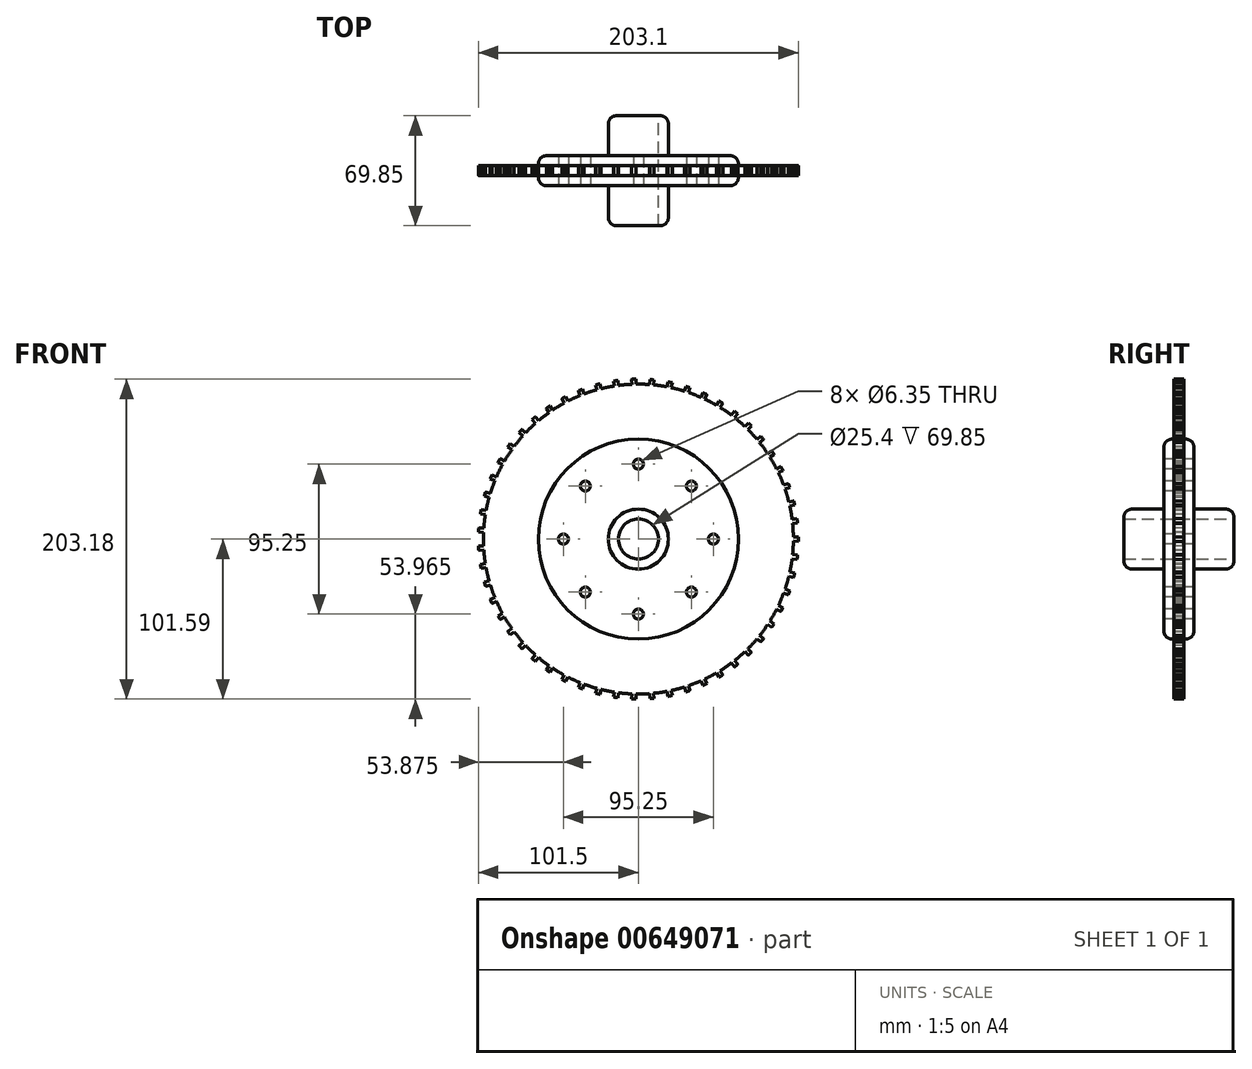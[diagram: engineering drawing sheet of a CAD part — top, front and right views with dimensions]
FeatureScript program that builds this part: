
annotation { "Feature Type Name" : "Feature", "Feature Type Description" : "" }
export const myFeature = defineFeature(function(context is Context, id is Id, definition is map)
    precondition{}
    {
        {
            var Q0;
            Q0=qCreatedBy(makeId("Front.planeOp"),FACE);
            var sketch = newSketch(context, id + "F0", { "sketchPlane" : qUnion([Q0])});
            skCircle(sketch, "E0", {"center": v(0, 0) * mm, "radius": 101.6 * mm});
            skCircle(sketch, "E1", {"center": v(0, 0) * mm, "radius": 12.7 * mm});
            skSolve(sketch);
        }
        {
            var Q0;
            Q0 = qSketchRegion(id + "F0", true);
            extrude(context, id + "F1", {"entities" : qUnion([Q0]), "depth" : 6.35 * mm, "offsetDistance" : 25.4 * mm});
        }
        {
            var Q0;
            Q0=makeQuery(id+"F1.opExtrude","CAP_FACE",FACE,{"disambiguationData":[OSD([sQuery(id+"F0.wireOp",EDGE,"E0"),sQuery(id+"F0.wireOp",EDGE,"E1")])],"isStart":false});
            var sketch = newSketch(context, id + "F2", { "sketchPlane" : qUnion([Q0])});
            skArc(sketch, "E2", {"start": v(-101.5, 4.43) * mm, "mid": v(-101.6, 0) * mm, "end": v(-101.5, -4.43) * mm});
            skArc(sketch, "E3", {"start": v(-98.33, 4.3) * mm, "mid": v(-98.43, 0) * mm, "end": v(-98.33, -4.3) * mm});
            skLineSegment(sketch, "E4", {"start": v(-98.33, -4.3) * mm, "end": v(-101.5, -4.43) * mm});
            skLineSegment(sketch, "E5", {"start": v(-101.5, -4.43) * mm, "end": v(-98.33, -4.3) * mm});
            skLineSegment(sketch, "E6", {"start": v(-101.5, 4.43) * mm, "end": v(-98.33, 4.3) * mm});
            skArc(sketch, "E7.1.0", {"start": v(-98.18, -6.94) * mm, "mid": v(-97.78, -11.22) * mm, "end": v(-97.2, -15.47) * mm});
            skLineSegment(sketch, "E7.1.1", {"start": v(-100.34, -15.97) * mm, "end": v(-97.2, -15.47) * mm});
            skLineSegment(sketch, "E7.1.2", {"start": v(-101.35, -7.17) * mm, "end": v(-98.18, -6.94) * mm});
            skArc(sketch, "E7.1.3", {"start": v(-101.35, -7.17) * mm, "mid": v(-100.94, -11.58) * mm, "end": v(-100.34, -15.97) * mm});
            skArc(sketch, "E7.2.0", {"start": v(-96.75, -18.1) * mm, "mid": v(-95.87, -22.3) * mm, "end": v(-94.8, -26.45) * mm});
            skLineSegment(sketch, "E7.2.1", {"start": v(-97.86, -27.3) * mm, "end": v(-94.8, -26.45) * mm});
            skLineSegment(sketch, "E7.2.2", {"start": v(-99.87, -18.67) * mm, "end": v(-96.75, -18.1) * mm});
            skArc(sketch, "E7.2.3", {"start": v(-99.87, -18.67) * mm, "mid": v(-98.96, -23.01) * mm, "end": v(-97.86, -27.3) * mm});
            skArc(sketch, "E7.3.0", {"start": v(-94.06, -29) * mm, "mid": v(-92.7, -33.08) * mm, "end": v(-91.17, -37.09) * mm});
            skLineSegment(sketch, "E7.3.1", {"start": v(-94.11, -38.28) * mm, "end": v(-91.17, -37.09) * mm});
            skLineSegment(sketch, "E7.3.2", {"start": v(-97.09, -29.94) * mm, "end": v(-94.06, -29) * mm});
            skArc(sketch, "E7.3.3", {"start": v(-97.09, -29.94) * mm, "mid": v(-95.7, -34.14) * mm, "end": v(-94.11, -38.28) * mm});
            skArc(sketch, "E7.4.0", {"start": v(-90.14, -39.53) * mm, "mid": v(-88.33, -43.43) * mm, "end": v(-86.35, -47.24) * mm});
            skLineSegment(sketch, "E7.4.1", {"start": v(-89.13, -48.76) * mm, "end": v(-86.35, -47.24) * mm});
            skLineSegment(sketch, "E7.4.2", {"start": v(-93.04, -40.8) * mm, "end": v(-90.14, -39.53) * mm});
            skArc(sketch, "E7.4.3", {"start": v(-93.04, -40.8) * mm, "mid": v(-91.18, -44.83) * mm, "end": v(-89.13, -48.76) * mm});
            skArc(sketch, "E7.5.0", {"start": v(-85.04, -49.55) * mm, "mid": v(-82.8, -53.21) * mm, "end": v(-80.4, -56.77) * mm});
            skLineSegment(sketch, "E7.5.1", {"start": v(-83, -58.6) * mm, "end": v(-80.4, -56.77) * mm});
            skLineSegment(sketch, "E7.5.2", {"start": v(-87.79, -51.15) * mm, "end": v(-85.04, -49.55) * mm});
            skArc(sketch, "E7.5.3", {"start": v(-87.79, -51.15) * mm, "mid": v(-85.47, -54.93) * mm, "end": v(-83, -58.6) * mm});
            skArc(sketch, "E7.6.0", {"start": v(-78.84, -58.92) * mm, "mid": v(-76.2, -62.3) * mm, "end": v(-73.4, -65.57) * mm});
            skLineSegment(sketch, "E7.6.1", {"start": v(-75.77, -67.68) * mm, "end": v(-73.4, -65.57) * mm});
            skLineSegment(sketch, "E7.6.2", {"start": v(-81.38, -60.82) * mm, "end": v(-78.84, -58.92) * mm});
            skArc(sketch, "E7.6.3", {"start": v(-81.38, -60.82) * mm, "mid": v(-78.65, -64.31) * mm, "end": v(-75.77, -67.68) * mm});
            skArc(sketch, "E7.7.0", {"start": v(-71.6, -67.52) * mm, "mid": v(-68.6, -70.58) * mm, "end": v(-65.45, -73.5) * mm});
            skLineSegment(sketch, "E7.7.1", {"start": v(-67.56, -75.88) * mm, "end": v(-65.45, -73.5) * mm});
            skLineSegment(sketch, "E7.7.2", {"start": v(-73.92, -69.7) * mm, "end": v(-71.6, -67.52) * mm});
            skArc(sketch, "E7.7.3", {"start": v(-73.92, -69.7) * mm, "mid": v(-70.8, -72.86) * mm, "end": v(-67.56, -75.88) * mm});
            skArc(sketch, "E7.8.0", {"start": v(-63.45, -75.25) * mm, "mid": v(-60.1, -77.94) * mm, "end": v(-56.65, -80.5) * mm});
            skLineSegment(sketch, "E7.8.1", {"start": v(-58.47, -83.09) * mm, "end": v(-56.65, -80.5) * mm});
            skLineSegment(sketch, "E7.8.2", {"start": v(-65.5, -77.67) * mm, "end": v(-63.45, -75.25) * mm});
            skArc(sketch, "E7.8.3", {"start": v(-65.5, -77.67) * mm, "mid": v(-62.04, -80.46) * mm, "end": v(-58.47, -83.09) * mm});
            skArc(sketch, "E7.9.0", {"start": v(-54.45, -81.99) * mm, "mid": v(-50.83, -84.29) * mm, "end": v(-47.1, -86.42) * mm});
            skLineSegment(sketch, "E7.9.1", {"start": v(-48.62, -89.21) * mm, "end": v(-47.1, -86.42) * mm});
            skLineSegment(sketch, "E7.9.2", {"start": v(-56.21, -84.63) * mm, "end": v(-54.45, -81.99) * mm});
            skArc(sketch, "E7.9.3", {"start": v(-56.21, -84.63) * mm, "mid": v(-52.47, -87) * mm, "end": v(-48.62, -89.21) * mm});
            skArc(sketch, "E7.10.0", {"start": v(-44.75, -87.66) * mm, "mid": v(-40.89, -89.53) * mm, "end": v(-36.94, -91.23) * mm});
            skLineSegment(sketch, "E7.10.1", {"start": v(-38.13, -94.17) * mm, "end": v(-36.94, -91.23) * mm});
            skLineSegment(sketch, "E7.10.2", {"start": v(-46.2, -90.49) * mm, "end": v(-44.75, -87.66) * mm});
            skArc(sketch, "E7.10.3", {"start": v(-46.2, -90.49) * mm, "mid": v(-42.2, -92.42) * mm, "end": v(-38.13, -94.17) * mm});
            skArc(sketch, "E7.11.0", {"start": v(-34.47, -92.2) * mm, "mid": v(-30.41, -93.6) * mm, "end": v(-26.3, -94.85) * mm});
            skLineSegment(sketch, "E7.11.1", {"start": v(-27.15, -97.9) * mm, "end": v(-26.3, -94.85) * mm});
            skLineSegment(sketch, "E7.11.2", {"start": v(-35.58, -95.17) * mm, "end": v(-34.47, -92.2) * mm});
            skArc(sketch, "E7.11.3", {"start": v(-35.58, -95.17) * mm, "mid": v(-31.4, -96.63) * mm, "end": v(-27.15, -97.9) * mm});
            skArc(sketch, "E7.12.0", {"start": v(-23.74, -95.52) * mm, "mid": v(-19.55, -96.46) * mm, "end": v(-15.32, -97.23) * mm});
            skLineSegment(sketch, "E7.12.1", {"start": v(-15.81, -100.36) * mm, "end": v(-15.32, -97.23) * mm});
            skLineSegment(sketch, "E7.12.2", {"start": v(-24.5, -98.6) * mm, "end": v(-23.74, -95.52) * mm});
            skArc(sketch, "E7.12.3", {"start": v(-24.5, -98.6) * mm, "mid": v(-20.18, -99.58) * mm, "end": v(-15.81, -100.36) * mm});
            skArc(sketch, "E7.13.0", {"start": v(-12.7, -97.6) * mm, "mid": v(-8.42, -98.06) * mm, "end": v(-4.14, -98.34) * mm});
            skLineSegment(sketch, "E7.13.1", {"start": v(-4.27, -101.51) * mm, "end": v(-4.14, -98.34) * mm});
            skLineSegment(sketch, "E7.13.2", {"start": v(-13.1, -100.75) * mm, "end": v(-12.7, -97.6) * mm});
            skArc(sketch, "E7.13.3", {"start": v(-13.1, -100.75) * mm, "mid": v(-8.7, -101.23) * mm, "end": v(-4.27, -101.51) * mm});
            skArc(sketch, "E7.14.0", {"start": v(-1.48, -98.41) * mm, "mid": v(2.81, -98.38) * mm, "end": v(7.1, -98.17) * mm});
            skLineSegment(sketch, "E7.14.1", {"start": v(7.33, -101.34) * mm, "end": v(7.1, -98.17) * mm});
            skLineSegment(sketch, "E7.14.2", {"start": v(-1.53, -101.59) * mm, "end": v(-1.48, -98.41) * mm});
            skArc(sketch, "E7.14.3", {"start": v(-1.53, -101.59) * mm, "mid": v(2.9, -101.56) * mm, "end": v(7.33, -101.34) * mm});
            skArc(sketch, "E7.15.0", {"start": v(9.74, -97.94) * mm, "mid": v(14, -97.42) * mm, "end": v(18.24, -96.72) * mm});
            skLineSegment(sketch, "E7.15.1", {"start": v(18.83, -99.84) * mm, "end": v(18.24, -96.72) * mm});
            skLineSegment(sketch, "E7.15.2", {"start": v(10.06, -101.1) * mm, "end": v(9.74, -97.94) * mm});
            skArc(sketch, "E7.15.3", {"start": v(10.06, -101.1) * mm, "mid": v(14.46, -100.57) * mm, "end": v(18.83, -99.84) * mm});
            skArc(sketch, "E7.16.0", {"start": v(20.85, -96.2) * mm, "mid": v(25.02, -95.2) * mm, "end": v(29.15, -94) * mm});
            skLineSegment(sketch, "E7.16.1", {"start": v(30.1, -97.04) * mm, "end": v(29.15, -94) * mm});
            skLineSegment(sketch, "E7.16.2", {"start": v(21.52, -99.3) * mm, "end": v(20.85, -96.2) * mm});
            skArc(sketch, "E7.16.3", {"start": v(21.52, -99.3) * mm, "mid": v(25.83, -98.26) * mm, "end": v(30.1, -97.04) * mm});
            skArc(sketch, "E7.17.0", {"start": v(31.67, -93.19) * mm, "mid": v(35.7, -91.72) * mm, "end": v(39.68, -90.07) * mm});
            skLineSegment(sketch, "E7.17.1", {"start": v(40.96, -92.98) * mm, "end": v(39.68, -90.07) * mm});
            skLineSegment(sketch, "E7.17.2", {"start": v(32.7, -96.2) * mm, "end": v(31.67, -93.19) * mm});
            skArc(sketch, "E7.17.3", {"start": v(32.7, -96.2) * mm, "mid": v(36.86, -94.68) * mm, "end": v(40.96, -92.98) * mm});
            skArc(sketch, "E7.18.0", {"start": v(42.1, -88.97) * mm, "mid": v(45.93, -87.05) * mm, "end": v(49.69, -84.96) * mm});
            skLineSegment(sketch, "E7.18.1", {"start": v(51.29, -87.7) * mm, "end": v(49.69, -84.96) * mm});
            skLineSegment(sketch, "E7.18.2", {"start": v(43.45, -91.84) * mm, "end": v(42.1, -88.97) * mm});
            skArc(sketch, "E7.18.3", {"start": v(43.45, -91.84) * mm, "mid": v(47.41, -89.86) * mm, "end": v(51.29, -87.7) * mm});
            skArc(sketch, "E7.19.0", {"start": v(51.96, -83.6) * mm, "mid": v(55.56, -81.25) * mm, "end": v(59.05, -78.75) * mm});
            skLineSegment(sketch, "E7.19.1", {"start": v(60.95, -81.29) * mm, "end": v(59.05, -78.75) * mm});
            skLineSegment(sketch, "E7.19.2", {"start": v(53.63, -86.29) * mm, "end": v(51.96, -83.6) * mm});
            skArc(sketch, "E7.19.3", {"start": v(53.63, -86.29) * mm, "mid": v(57.35, -83.87) * mm, "end": v(60.95, -81.29) * mm});
            skArc(sketch, "E7.20.0", {"start": v(61.15, -77.13) * mm, "mid": v(64.45, -74.38) * mm, "end": v(67.64, -71.5) * mm});
            skLineSegment(sketch, "E7.20.1", {"start": v(69.82, -73.8) * mm, "end": v(67.64, -71.5) * mm});
            skLineSegment(sketch, "E7.20.2", {"start": v(63.12, -79.61) * mm, "end": v(61.15, -77.13) * mm});
            skArc(sketch, "E7.20.3", {"start": v(63.12, -79.61) * mm, "mid": v(66.53, -76.78) * mm, "end": v(69.82, -73.8) * mm});
            skArc(sketch, "E7.21.0", {"start": v(69.54, -69.65) * mm, "mid": v(72.51, -66.55) * mm, "end": v(75.35, -63.33) * mm});
            skLineSegment(sketch, "E7.21.1", {"start": v(77.78, -65.37) * mm, "end": v(75.35, -63.33) * mm});
            skLineSegment(sketch, "E7.21.2", {"start": v(71.79, -71.9) * mm, "end": v(69.54, -69.65) * mm});
            skArc(sketch, "E7.21.3", {"start": v(71.79, -71.9) * mm, "mid": v(74.85, -68.7) * mm, "end": v(77.78, -65.37) * mm});
            skArc(sketch, "E7.22.0", {"start": v(77.03, -61.27) * mm, "mid": v(79.63, -57.85) * mm, "end": v(82.08, -54.32) * mm});
            skLineSegment(sketch, "E7.22.1", {"start": v(84.72, -56.08) * mm, "end": v(82.08, -54.32) * mm});
            skLineSegment(sketch, "E7.22.2", {"start": v(79.51, -63.25) * mm, "end": v(77.03, -61.27) * mm});
            skArc(sketch, "E7.22.3", {"start": v(79.51, -63.25) * mm, "mid": v(82.2, -59.72) * mm, "end": v(84.72, -56.08) * mm});
            skArc(sketch, "E7.23.0", {"start": v(83.51, -52.1) * mm, "mid": v(85.7, -48.4) * mm, "end": v(87.73, -44.61) * mm});
            skLineSegment(sketch, "E7.23.1", {"start": v(90.56, -46.05) * mm, "end": v(87.73, -44.61) * mm});
            skLineSegment(sketch, "E7.23.2", {"start": v(86.2, -53.77) * mm, "end": v(83.51, -52.1) * mm});
            skArc(sketch, "E7.23.3", {"start": v(86.2, -53.77) * mm, "mid": v(88.47, -49.96) * mm, "end": v(90.56, -46.05) * mm});
            skArc(sketch, "E7.24.0", {"start": v(88.9, -42.23) * mm, "mid": v(90.66, -38.31) * mm, "end": v(92.25, -34.32) * mm});
            skLineSegment(sketch, "E7.24.1", {"start": v(95.22, -35.43) * mm, "end": v(92.25, -34.32) * mm});
            skLineSegment(sketch, "E7.24.2", {"start": v(91.77, -43.6) * mm, "end": v(88.9, -42.23) * mm});
            skArc(sketch, "E7.24.3", {"start": v(91.77, -43.6) * mm, "mid": v(93.59, -39.55) * mm, "end": v(95.22, -35.43) * mm});
            skArc(sketch, "E7.25.0", {"start": v(93.14, -31.82) * mm, "mid": v(94.44, -27.73) * mm, "end": v(95.56, -23.58) * mm});
            skLineSegment(sketch, "E7.25.1", {"start": v(98.64, -24.34) * mm, "end": v(95.56, -23.58) * mm});
            skLineSegment(sketch, "E7.25.2", {"start": v(96.14, -32.85) * mm, "end": v(93.14, -31.82) * mm});
            skArc(sketch, "E7.25.3", {"start": v(96.14, -32.85) * mm, "mid": v(97.48, -28.62) * mm, "end": v(98.64, -24.34) * mm});
            skArc(sketch, "E7.26.0", {"start": v(96.16, -21) * mm, "mid": v(96.98, -16.78) * mm, "end": v(97.62, -12.54) * mm});
            skLineSegment(sketch, "E7.26.1", {"start": v(100.77, -12.94) * mm, "end": v(97.62, -12.54) * mm});
            skLineSegment(sketch, "E7.26.2", {"start": v(99.26, -21.68) * mm, "end": v(96.16, -21) * mm});
            skArc(sketch, "E7.26.3", {"start": v(99.26, -21.68) * mm, "mid": v(100.11, -17.33) * mm, "end": v(100.77, -12.94) * mm});
            skArc(sketch, "E7.27.0", {"start": v(97.93, -9.9) * mm, "mid": v(98.26, -5.62) * mm, "end": v(98.42, -1.33) * mm});
            skLineSegment(sketch, "E7.27.1", {"start": v(101.6, -1.37) * mm, "end": v(98.42, -1.33) * mm});
            skLineSegment(sketch, "E7.27.2", {"start": v(101.08, -10.22) * mm, "end": v(97.93, -9.9) * mm});
            skArc(sketch, "E7.27.3", {"start": v(101.08, -10.22) * mm, "mid": v(101.43, -5.8) * mm, "end": v(101.6, -1.37) * mm});
            skArc(sketch, "E7.28.0", {"start": v(98.42, 1.33) * mm, "mid": v(98.26, 5.62) * mm, "end": v(97.93, 9.9) * mm});
            skLineSegment(sketch, "E7.28.1", {"start": v(101.08, 10.22) * mm, "end": v(97.93, 9.9) * mm});
            skLineSegment(sketch, "E7.28.2", {"start": v(101.6, 1.37) * mm, "end": v(98.42, 1.33) * mm});
            skArc(sketch, "E7.28.3", {"start": v(101.6, 1.37) * mm, "mid": v(101.43, 5.8) * mm, "end": v(101.08, 10.22) * mm});
            skArc(sketch, "E7.29.0", {"start": v(97.62, 12.54) * mm, "mid": v(96.98, 16.78) * mm, "end": v(96.16, 21) * mm});
            skLineSegment(sketch, "E7.29.1", {"start": v(99.26, 21.68) * mm, "end": v(96.16, 21) * mm});
            skLineSegment(sketch, "E7.29.2", {"start": v(100.77, 12.94) * mm, "end": v(97.62, 12.54) * mm});
            skArc(sketch, "E7.29.3", {"start": v(100.77, 12.94) * mm, "mid": v(100.11, 17.33) * mm, "end": v(99.26, 21.68) * mm});
            skArc(sketch, "E7.30.0", {"start": v(95.56, 23.58) * mm, "mid": v(94.44, 27.73) * mm, "end": v(93.14, 31.82) * mm});
            skLineSegment(sketch, "E7.30.1", {"start": v(96.14, 32.85) * mm, "end": v(93.14, 31.82) * mm});
            skLineSegment(sketch, "E7.30.2", {"start": v(98.64, 24.34) * mm, "end": v(95.56, 23.58) * mm});
            skArc(sketch, "E7.30.3", {"start": v(98.64, 24.34) * mm, "mid": v(97.48, 28.62) * mm, "end": v(96.14, 32.85) * mm});
            skArc(sketch, "E7.31.0", {"start": v(92.25, 34.32) * mm, "mid": v(90.66, 38.31) * mm, "end": v(88.9, 42.23) * mm});
            skLineSegment(sketch, "E7.31.1", {"start": v(91.77, 43.6) * mm, "end": v(88.9, 42.23) * mm});
            skLineSegment(sketch, "E7.31.2", {"start": v(95.22, 35.43) * mm, "end": v(92.25, 34.32) * mm});
            skArc(sketch, "E7.31.3", {"start": v(95.22, 35.43) * mm, "mid": v(93.59, 39.55) * mm, "end": v(91.77, 43.6) * mm});
            skArc(sketch, "E7.32.0", {"start": v(87.73, 44.61) * mm, "mid": v(85.7, 48.4) * mm, "end": v(83.51, 52.1) * mm});
            skLineSegment(sketch, "E7.32.1", {"start": v(86.2, 53.77) * mm, "end": v(83.51, 52.1) * mm});
            skLineSegment(sketch, "E7.32.2", {"start": v(90.56, 46.05) * mm, "end": v(87.73, 44.61) * mm});
            skArc(sketch, "E7.32.3", {"start": v(90.56, 46.05) * mm, "mid": v(88.47, 49.96) * mm, "end": v(86.2, 53.77) * mm});
            skArc(sketch, "E7.33.0", {"start": v(82.08, 54.32) * mm, "mid": v(79.63, 57.85) * mm, "end": v(77.03, 61.27) * mm});
            skLineSegment(sketch, "E7.33.1", {"start": v(79.51, 63.25) * mm, "end": v(77.03, 61.27) * mm});
            skLineSegment(sketch, "E7.33.2", {"start": v(84.72, 56.08) * mm, "end": v(82.08, 54.32) * mm});
            skArc(sketch, "E7.33.3", {"start": v(84.72, 56.08) * mm, "mid": v(82.2, 59.72) * mm, "end": v(79.51, 63.25) * mm});
            skArc(sketch, "E7.34.0", {"start": v(75.35, 63.33) * mm, "mid": v(72.51, 66.55) * mm, "end": v(69.54, 69.65) * mm});
            skLineSegment(sketch, "E7.34.1", {"start": v(71.79, 71.9) * mm, "end": v(69.54, 69.65) * mm});
            skLineSegment(sketch, "E7.34.2", {"start": v(77.78, 65.37) * mm, "end": v(75.35, 63.33) * mm});
            skArc(sketch, "E7.34.3", {"start": v(77.78, 65.37) * mm, "mid": v(74.85, 68.7) * mm, "end": v(71.79, 71.9) * mm});
            skArc(sketch, "E7.35.0", {"start": v(67.64, 71.5) * mm, "mid": v(64.45, 74.38) * mm, "end": v(61.15, 77.13) * mm});
            skLineSegment(sketch, "E7.35.1", {"start": v(63.12, 79.61) * mm, "end": v(61.15, 77.13) * mm});
            skLineSegment(sketch, "E7.35.2", {"start": v(69.82, 73.8) * mm, "end": v(67.64, 71.5) * mm});
            skArc(sketch, "E7.35.3", {"start": v(69.82, 73.8) * mm, "mid": v(66.53, 76.78) * mm, "end": v(63.12, 79.61) * mm});
            skArc(sketch, "E7.36.0", {"start": v(59.05, 78.75) * mm, "mid": v(55.56, 81.25) * mm, "end": v(51.96, 83.6) * mm});
            skLineSegment(sketch, "E7.36.1", {"start": v(53.63, 86.29) * mm, "end": v(51.96, 83.6) * mm});
            skLineSegment(sketch, "E7.36.2", {"start": v(60.95, 81.29) * mm, "end": v(59.05, 78.75) * mm});
            skArc(sketch, "E7.36.3", {"start": v(60.95, 81.29) * mm, "mid": v(57.35, 83.87) * mm, "end": v(53.63, 86.29) * mm});
            skArc(sketch, "E7.37.0", {"start": v(49.69, 84.96) * mm, "mid": v(45.93, 87.05) * mm, "end": v(42.1, 88.97) * mm});
            skLineSegment(sketch, "E7.37.1", {"start": v(43.45, 91.84) * mm, "end": v(42.1, 88.97) * mm});
            skLineSegment(sketch, "E7.37.2", {"start": v(51.29, 87.7) * mm, "end": v(49.69, 84.96) * mm});
            skArc(sketch, "E7.37.3", {"start": v(51.29, 87.7) * mm, "mid": v(47.41, 89.86) * mm, "end": v(43.45, 91.84) * mm});
            skArc(sketch, "E7.38.0", {"start": v(39.68, 90.07) * mm, "mid": v(35.7, 91.72) * mm, "end": v(31.67, 93.19) * mm});
            skLineSegment(sketch, "E7.38.1", {"start": v(32.7, 96.2) * mm, "end": v(31.67, 93.19) * mm});
            skLineSegment(sketch, "E7.38.2", {"start": v(40.96, 92.98) * mm, "end": v(39.68, 90.07) * mm});
            skArc(sketch, "E7.38.3", {"start": v(40.96, 92.98) * mm, "mid": v(36.86, 94.68) * mm, "end": v(32.7, 96.2) * mm});
            skArc(sketch, "E7.39.0", {"start": v(29.15, 94) * mm, "mid": v(25.02, 95.2) * mm, "end": v(20.85, 96.2) * mm});
            skLineSegment(sketch, "E7.39.1", {"start": v(21.52, 99.3) * mm, "end": v(20.85, 96.2) * mm});
            skLineSegment(sketch, "E7.39.2", {"start": v(30.1, 97.04) * mm, "end": v(29.15, 94) * mm});
            skArc(sketch, "E7.39.3", {"start": v(30.1, 97.04) * mm, "mid": v(25.83, 98.26) * mm, "end": v(21.52, 99.3) * mm});
            skArc(sketch, "E7.40.0", {"start": v(18.24, 96.72) * mm, "mid": v(14, 97.42) * mm, "end": v(9.74, 97.94) * mm});
            skLineSegment(sketch, "E7.40.1", {"start": v(10.06, 101.1) * mm, "end": v(9.74, 97.94) * mm});
            skLineSegment(sketch, "E7.40.2", {"start": v(18.83, 99.84) * mm, "end": v(18.24, 96.72) * mm});
            skArc(sketch, "E7.40.3", {"start": v(18.83, 99.84) * mm, "mid": v(14.46, 100.57) * mm, "end": v(10.06, 101.1) * mm});
            skArc(sketch, "E7.41.0", {"start": v(7.1, 98.17) * mm, "mid": v(2.81, 98.38) * mm, "end": v(-1.48, 98.41) * mm});
            skLineSegment(sketch, "E7.41.1", {"start": v(-1.53, 101.59) * mm, "end": v(-1.48, 98.41) * mm});
            skLineSegment(sketch, "E7.41.2", {"start": v(7.33, 101.34) * mm, "end": v(7.1, 98.17) * mm});
            skArc(sketch, "E7.41.3", {"start": v(7.33, 101.34) * mm, "mid": v(2.9, 101.56) * mm, "end": v(-1.53, 101.59) * mm});
            skArc(sketch, "E7.42.0", {"start": v(-4.14, 98.34) * mm, "mid": v(-8.42, 98.06) * mm, "end": v(-12.7, 97.6) * mm});
            skLineSegment(sketch, "E7.42.1", {"start": v(-13.1, 100.75) * mm, "end": v(-12.7, 97.6) * mm});
            skLineSegment(sketch, "E7.42.2", {"start": v(-4.27, 101.51) * mm, "end": v(-4.14, 98.34) * mm});
            skArc(sketch, "E7.42.3", {"start": v(-4.27, 101.51) * mm, "mid": v(-8.7, 101.23) * mm, "end": v(-13.1, 100.75) * mm});
            skArc(sketch, "E7.43.0", {"start": v(-15.32, 97.23) * mm, "mid": v(-19.55, 96.46) * mm, "end": v(-23.74, 95.52) * mm});
            skLineSegment(sketch, "E7.43.1", {"start": v(-24.5, 98.6) * mm, "end": v(-23.74, 95.52) * mm});
            skLineSegment(sketch, "E7.43.2", {"start": v(-15.81, 100.36) * mm, "end": v(-15.32, 97.23) * mm});
            skArc(sketch, "E7.43.3", {"start": v(-15.81, 100.36) * mm, "mid": v(-20.18, 99.58) * mm, "end": v(-24.5, 98.6) * mm});
            skArc(sketch, "E7.44.0", {"start": v(-26.3, 94.85) * mm, "mid": v(-30.41, 93.6) * mm, "end": v(-34.47, 92.2) * mm});
            skLineSegment(sketch, "E7.44.1", {"start": v(-35.58, 95.17) * mm, "end": v(-34.47, 92.2) * mm});
            skLineSegment(sketch, "E7.44.2", {"start": v(-27.15, 97.9) * mm, "end": v(-26.3, 94.85) * mm});
            skArc(sketch, "E7.44.3", {"start": v(-27.15, 97.9) * mm, "mid": v(-31.4, 96.63) * mm, "end": v(-35.58, 95.17) * mm});
            skArc(sketch, "E7.45.0", {"start": v(-36.94, 91.23) * mm, "mid": v(-40.89, 89.53) * mm, "end": v(-44.75, 87.66) * mm});
            skLineSegment(sketch, "E7.45.1", {"start": v(-46.2, 90.49) * mm, "end": v(-44.75, 87.66) * mm});
            skLineSegment(sketch, "E7.45.2", {"start": v(-38.13, 94.17) * mm, "end": v(-36.94, 91.23) * mm});
            skArc(sketch, "E7.45.3", {"start": v(-38.13, 94.17) * mm, "mid": v(-42.2, 92.42) * mm, "end": v(-46.2, 90.49) * mm});
            skArc(sketch, "E7.46.0", {"start": v(-47.1, 86.42) * mm, "mid": v(-50.83, 84.29) * mm, "end": v(-54.45, 81.99) * mm});
            skLineSegment(sketch, "E7.46.1", {"start": v(-56.21, 84.63) * mm, "end": v(-54.45, 81.99) * mm});
            skLineSegment(sketch, "E7.46.2", {"start": v(-48.62, 89.21) * mm, "end": v(-47.1, 86.42) * mm});
            skArc(sketch, "E7.46.3", {"start": v(-48.62, 89.21) * mm, "mid": v(-52.47, 87) * mm, "end": v(-56.21, 84.63) * mm});
            skArc(sketch, "E7.47.0", {"start": v(-56.65, 80.5) * mm, "mid": v(-60.1, 77.94) * mm, "end": v(-63.45, 75.25) * mm});
            skLineSegment(sketch, "E7.47.1", {"start": v(-65.5, 77.67) * mm, "end": v(-63.45, 75.25) * mm});
            skLineSegment(sketch, "E7.47.2", {"start": v(-58.47, 83.09) * mm, "end": v(-56.65, 80.5) * mm});
            skArc(sketch, "E7.47.3", {"start": v(-58.47, 83.09) * mm, "mid": v(-62.04, 80.46) * mm, "end": v(-65.5, 77.67) * mm});
            skArc(sketch, "E7.48.0", {"start": v(-65.45, 73.5) * mm, "mid": v(-68.6, 70.58) * mm, "end": v(-71.6, 67.52) * mm});
            skLineSegment(sketch, "E7.48.1", {"start": v(-73.92, 69.7) * mm, "end": v(-71.6, 67.52) * mm});
            skLineSegment(sketch, "E7.48.2", {"start": v(-67.56, 75.88) * mm, "end": v(-65.45, 73.5) * mm});
            skArc(sketch, "E7.48.3", {"start": v(-67.56, 75.88) * mm, "mid": v(-70.8, 72.86) * mm, "end": v(-73.92, 69.7) * mm});
            skArc(sketch, "E7.49.0", {"start": v(-73.4, 65.57) * mm, "mid": v(-76.2, 62.3) * mm, "end": v(-78.84, 58.92) * mm});
            skLineSegment(sketch, "E7.49.1", {"start": v(-81.38, 60.82) * mm, "end": v(-78.84, 58.92) * mm});
            skLineSegment(sketch, "E7.49.2", {"start": v(-75.77, 67.68) * mm, "end": v(-73.4, 65.57) * mm});
            skArc(sketch, "E7.49.3", {"start": v(-75.77, 67.68) * mm, "mid": v(-78.65, 64.31) * mm, "end": v(-81.38, 60.82) * mm});
            skArc(sketch, "E7.50.0", {"start": v(-80.4, 56.77) * mm, "mid": v(-82.8, 53.21) * mm, "end": v(-85.04, 49.55) * mm});
            skLineSegment(sketch, "E7.50.1", {"start": v(-87.79, 51.15) * mm, "end": v(-85.04, 49.55) * mm});
            skLineSegment(sketch, "E7.50.2", {"start": v(-83, 58.6) * mm, "end": v(-80.4, 56.77) * mm});
            skArc(sketch, "E7.50.3", {"start": v(-83, 58.6) * mm, "mid": v(-85.47, 54.93) * mm, "end": v(-87.79, 51.15) * mm});
            skArc(sketch, "E7.51.0", {"start": v(-86.35, 47.24) * mm, "mid": v(-88.33, 43.43) * mm, "end": v(-90.14, 39.53) * mm});
            skLineSegment(sketch, "E7.51.1", {"start": v(-93.04, 40.8) * mm, "end": v(-90.14, 39.53) * mm});
            skLineSegment(sketch, "E7.51.2", {"start": v(-89.13, 48.76) * mm, "end": v(-86.35, 47.24) * mm});
            skArc(sketch, "E7.51.3", {"start": v(-89.13, 48.76) * mm, "mid": v(-91.18, 44.83) * mm, "end": v(-93.04, 40.8) * mm});
            skArc(sketch, "E7.52.0", {"start": v(-91.17, 37.09) * mm, "mid": v(-92.7, 33.08) * mm, "end": v(-94.06, 29) * mm});
            skLineSegment(sketch, "E7.52.1", {"start": v(-97.09, 29.94) * mm, "end": v(-94.06, 29) * mm});
            skLineSegment(sketch, "E7.52.2", {"start": v(-94.11, 38.28) * mm, "end": v(-91.17, 37.09) * mm});
            skArc(sketch, "E7.52.3", {"start": v(-94.11, 38.28) * mm, "mid": v(-95.7, 34.14) * mm, "end": v(-97.09, 29.94) * mm});
            skArc(sketch, "E7.53.0", {"start": v(-94.8, 26.45) * mm, "mid": v(-95.87, 22.3) * mm, "end": v(-96.75, 18.1) * mm});
            skLineSegment(sketch, "E7.53.1", {"start": v(-99.87, 18.67) * mm, "end": v(-96.75, 18.1) * mm});
            skLineSegment(sketch, "E7.53.2", {"start": v(-97.86, 27.3) * mm, "end": v(-94.8, 26.45) * mm});
            skArc(sketch, "E7.53.3", {"start": v(-97.86, 27.3) * mm, "mid": v(-98.96, 23.01) * mm, "end": v(-99.87, 18.67) * mm});
            skArc(sketch, "E7.54.0", {"start": v(-97.2, 15.47) * mm, "mid": v(-97.78, 11.22) * mm, "end": v(-98.18, 6.94) * mm});
            skLineSegment(sketch, "E7.54.1", {"start": v(-101.35, 7.17) * mm, "end": v(-98.18, 6.94) * mm});
            skLineSegment(sketch, "E7.54.2", {"start": v(-100.34, 15.97) * mm, "end": v(-97.2, 15.47) * mm});
            skArc(sketch, "E7.54.3", {"start": v(-100.34, 15.97) * mm, "mid": v(-100.94, 11.58) * mm, "end": v(-101.35, 7.17) * mm});
            skSolve(sketch);
        }
        {
            var Q0;
            Q0 = qSketchRegion(id + "F2", true);
            extrude(context, id + "F3", {"entities" : qUnion([Q0]), "operationType" : NewBodyOperationType.REMOVE, "oppositeDirection" : true, "depth" : 25.4 * mm, "offsetDistance" : 25.4 * mm});
        }
        {
            var Q0;
            Q0=makeQuery(id+"F1.opExtrude","CAP_FACE",FACE,{"disambiguationData":[OSD([sQuery(id+"F0.wireOp",EDGE,"E0"),sQuery(id+"F0.wireOp",EDGE,"E1")])],"isStart":false});
            var sketch = newSketch(context, id + "F4", { "sketchPlane" : qUnion([Q0])});
            skCircle(sketch, "E8", {"center": v(0, 0) * mm, "radius": 63.5 * mm});
            skCircle(sketch, "E9", {"center": v(0, 0) * mm, "radius": 12.7 * mm});
            skSolve(sketch);
        }
        {
            var Q0;
            Q0 = qSketchRegion(id + "F4", true);
            extrude(context, id + "F5", {"entities" : qUnion([Q0]), "operationType" : NewBodyOperationType.ADD, "depth" : 6.35 * mm, "offsetDistance" : 25.4 * mm});
        }
        {
            var Q0;
            Q0=makeQuery(id+"F5.opExtrude","CAP_FACE",FACE,{"disambiguationData":[OSD([sQuery(id+"F4.wireOp",EDGE,"E8"),sQuery(id+"F4.wireOp",EDGE,"E9")])],"isStart":false});
            var sketch = newSketch(context, id + "F6", { "sketchPlane" : qUnion([Q0])});
            skCircle(sketch, "E10", {"center": v(-47.63, 0) * mm, "radius": 3.18 * mm});
            skCircle(sketch, "E11.1.0", {"center": v(-33.68, -33.68) * mm, "radius": 3.18 * mm});
            skCircle(sketch, "E11.2.0", {"center": v(0, -47.63) * mm, "radius": 3.18 * mm});
            skCircle(sketch, "E11.3.0", {"center": v(33.68, -33.68) * mm, "radius": 3.18 * mm});
            skCircle(sketch, "E11.4.0", {"center": v(47.63, 0) * mm, "radius": 3.18 * mm});
            skCircle(sketch, "E11.5.0", {"center": v(33.68, 33.68) * mm, "radius": 3.18 * mm});
            skCircle(sketch, "E11.6.0", {"center": v(0, 47.63) * mm, "radius": 3.18 * mm});
            skCircle(sketch, "E11.7.0", {"center": v(-33.68, 33.68) * mm, "radius": 3.18 * mm});
            skPoint(sketch, "E11.center", {"position": v(0, 0) * mm});
            skSolve(sketch);
        }
        {
            var Q0;
            Q0 = qSketchRegion(id + "F6", true);
            extrude(context, id + "F7", {"entities" : qUnion([Q0]), "operationType" : NewBodyOperationType.REMOVE, "oppositeDirection" : true, "depth" : 25.4 * mm, "offsetDistance" : 25.4 * mm});
        }
        {
            var Q0;
            Q0=makeQuery(id+"F5.opExtrude","CAP_FACE",FACE,{"disambiguationData":[OSD([sQuery(id+"F4.wireOp",EDGE,"E8"),sQuery(id+"F4.wireOp",EDGE,"E9")])],"isStart":false});
            var sketch = newSketch(context, id + "F8", { "sketchPlane" : qUnion([Q0])});
            skCircle(sketch, "E12", {"center": v(0, 0) * mm, "radius": 19.05 * mm});
            skCircle(sketch, "E13", {"center": v(0, 0) * mm, "radius": 12.7 * mm});
            skSolve(sketch);
        }
        {
            var Q0;
            Q0 = qSketchRegion(id + "F8", true);
            extrude(context, id + "F9", {"entities" : qUnion([Q0]), "operationType" : NewBodyOperationType.ADD, "depth" : 25.4 * mm, "offsetDistance" : 25.4 * mm});
        }
        {
            var Q0;
            Q0=makeQuery(id+"F5.opExtrude","CAP_EDGE",EDGE,{"disambiguationData":[OSD([sQuery(id+"F4.wireOp",EDGE,"E8")])],"isStart":false});
            var Q1;
            Q1=makeQuery(id+"F9.opExtrude","CAP_EDGE",EDGE,{"disambiguationData":[OSD([sQuery(id+"F8.wireOp",EDGE,"E12")])],"isStart":false});
            fillet(context, id + "F10", {"entities" : qUnion([Q0, Q1]), "radius" : 5.08 * mm, "tangentPropagation" : true, "allowEdgeOverflow" : false});
        }
        {
            var Q0;
            Q0=makeQuery(id+"F1.opExtrude","CAP_FACE",FACE,{"disambiguationData":[OSD([sQuery(id+"F0.wireOp",EDGE,"E0"),sQuery(id+"F0.wireOp",EDGE,"E1")])],"isStart":true});
            var sketch = newSketch(context, id + "F11", { "sketchPlane" : qUnion([Q0])});
            skCircle(sketch, "E14", {"center": v(0, 0) * mm, "radius": 63.5 * mm});
            skCircle(sketch, "E15", {"center": v(0, 0) * mm, "radius": 12.7 * mm});
            skSolve(sketch);
        }
        {
            var Q0;
            Q0 = qSketchRegion(id + "F11", true);
            extrude(context, id + "F12", {"entities" : qUnion([Q0]), "operationType" : NewBodyOperationType.ADD, "depth" : 6.35 * mm, "offsetDistance" : 25.4 * mm});
        }
        {
            var Q0;
            Q0=makeQuery(id+"F12.opExtrude","CAP_FACE",FACE,{"disambiguationData":[OSD([sQuery(id+"F11.wireOp",EDGE,"E14"),sQuery(id+"F11.wireOp",EDGE,"E15")])],"isStart":false});
            var sketch = newSketch(context, id + "F13", { "sketchPlane" : qUnion([Q0])});
            skCircle(sketch, "E16", {"center": v(-47.63, 0) * mm, "radius": 3.18 * mm});
            skCircle(sketch, "E17.1.0", {"center": v(-33.68, -33.68) * mm, "radius": 3.18 * mm});
            skCircle(sketch, "E17.2.0", {"center": v(0, -47.63) * mm, "radius": 3.18 * mm});
            skCircle(sketch, "E17.3.0", {"center": v(33.68, -33.68) * mm, "radius": 3.18 * mm});
            skCircle(sketch, "E17.4.0", {"center": v(47.63, 0) * mm, "radius": 3.18 * mm});
            skCircle(sketch, "E17.5.0", {"center": v(33.68, 33.68) * mm, "radius": 3.18 * mm});
            skCircle(sketch, "E17.6.0", {"center": v(0, 47.63) * mm, "radius": 3.18 * mm});
            skCircle(sketch, "E17.7.0", {"center": v(-33.68, 33.68) * mm, "radius": 3.18 * mm});
            skPoint(sketch, "E17.center", {"position": v(0, 0) * mm});
            skSolve(sketch);
        }
        {
            var Q0;
            Q0 = qSketchRegion(id + "F13", true);
            extrude(context, id + "F14", {"entities" : qUnion([Q0]), "operationType" : NewBodyOperationType.REMOVE, "oppositeDirection" : true, "depth" : 25.4 * mm, "offsetDistance" : 25.4 * mm});
        }
        {
            var Q0;
            Q0=makeQuery(id+"F12.opExtrude","CAP_FACE",FACE,{"disambiguationData":[OSD([sQuery(id+"F11.wireOp",EDGE,"E14"),sQuery(id+"F11.wireOp",EDGE,"E15")])],"isStart":false});
            var sketch = newSketch(context, id + "F15", { "sketchPlane" : qUnion([Q0])});
            skCircle(sketch, "E18", {"center": v(0, 0) * mm, "radius": 19.05 * mm});
            skCircle(sketch, "E19", {"center": v(0, 0) * mm, "radius": 12.7 * mm});
            skSolve(sketch);
        }
        {
            var Q0;
            Q0 = qSketchRegion(id + "F15", true);
            extrude(context, id + "F16", {"entities" : qUnion([Q0]), "operationType" : NewBodyOperationType.ADD, "depth" : 25.4 * mm, "offsetDistance" : 25.4 * mm});
        }
        {
            var Q0;
            Q0=makeQuery(id+"F12.opExtrude","CAP_EDGE",EDGE,{"disambiguationData":[OSD([sQuery(id+"F11.wireOp",EDGE,"E14")])],"isStart":false});
            var Q1;
            Q1=makeQuery(id+"F16.opExtrude","CAP_EDGE",EDGE,{"disambiguationData":[OSD([sQuery(id+"F15.wireOp",EDGE,"E18")])],"isStart":false});
            fillet(context, id + "F17", {"entities" : qUnion([Q0, Q1]), "radius" : 5.08 * mm, "tangentPropagation" : true, "allowEdgeOverflow" : false});
        }
    });
